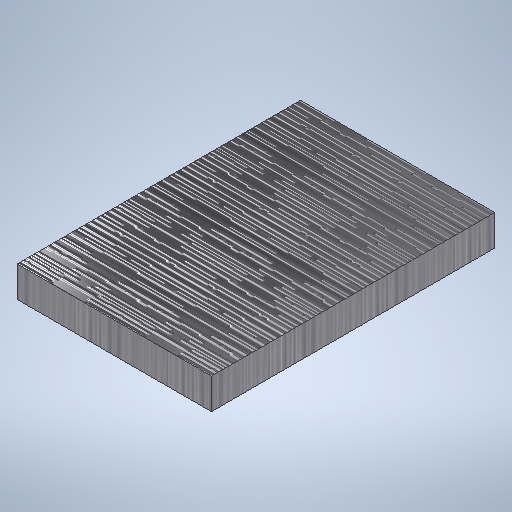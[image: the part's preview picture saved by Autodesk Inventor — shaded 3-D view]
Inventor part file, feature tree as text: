
AUTODESK INVENTOR PART (.ipt)
format: ipt  version: 2025.1 (Build 291241020, 241B)  size: 309,760 bytes
history: native  units: in
note: dims shown in document units (in); Inventor stores cm internally (conversion verified against a paired STEP export)
features: extrude x1, sketch x1
ambient origin geometry x8: Origin, YZ Plane, XZ Plane, XY Plane, X Axis, Y Axis, Z Axis, Center Point
bodies: Solid1 (feature_tree)
feature tree (2):
  extrude  "Extrusion1"  Depth=1.378in
  sketch  "Sketch1"  dims[d0=0.9449in d1=1.378in d2=0.15in d3=0.0in]
